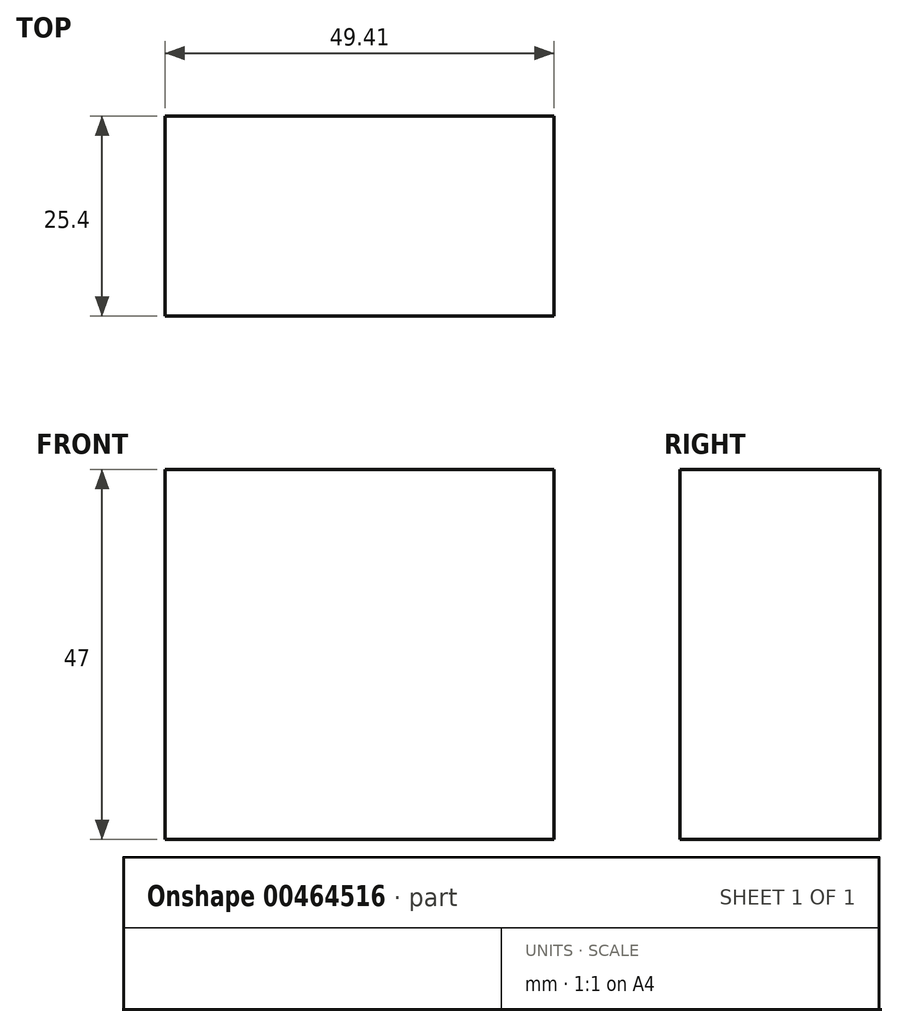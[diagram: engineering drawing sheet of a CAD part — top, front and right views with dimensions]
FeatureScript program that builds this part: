
annotation { "Feature Type Name" : "Feature", "Feature Type Description" : "" }
export const myFeature = defineFeature(function(context is Context, id is Id, definition is map)
    precondition{}
    {
        {
            var Q0;
            Q0=qCreatedBy(makeId("Front.planeOp"),FACE);
            var sketch = newSketch(context, id + "F0", { "sketchPlane" : qUnion([Q0])});
            skLineSegment(sketch, "E0.bottom", {"start": v(-7.48, 13.9) * mm, "end": v(41.93, 13.9) * mm});
            skLineSegment(sketch, "E0.top", {"start": v(-7.48, -33.1) * mm, "end": v(41.93, -33.1) * mm});
            skLineSegment(sketch, "E0.left", {"start": v(-7.48, 13.9) * mm, "end": v(-7.48, -33.1) * mm});
            skLineSegment(sketch, "E0.right", {"start": v(41.93, 13.9) * mm, "end": v(41.93, -33.1) * mm});
            skSolve(sketch);
        }
        {
            var Q0;
            Q0 = qSketchRegion(id + "F0", true);
            extrude(context, id + "F1", {"entities" : qUnion([Q0]), "depth" : 25.4 * mm});
        }
    });
